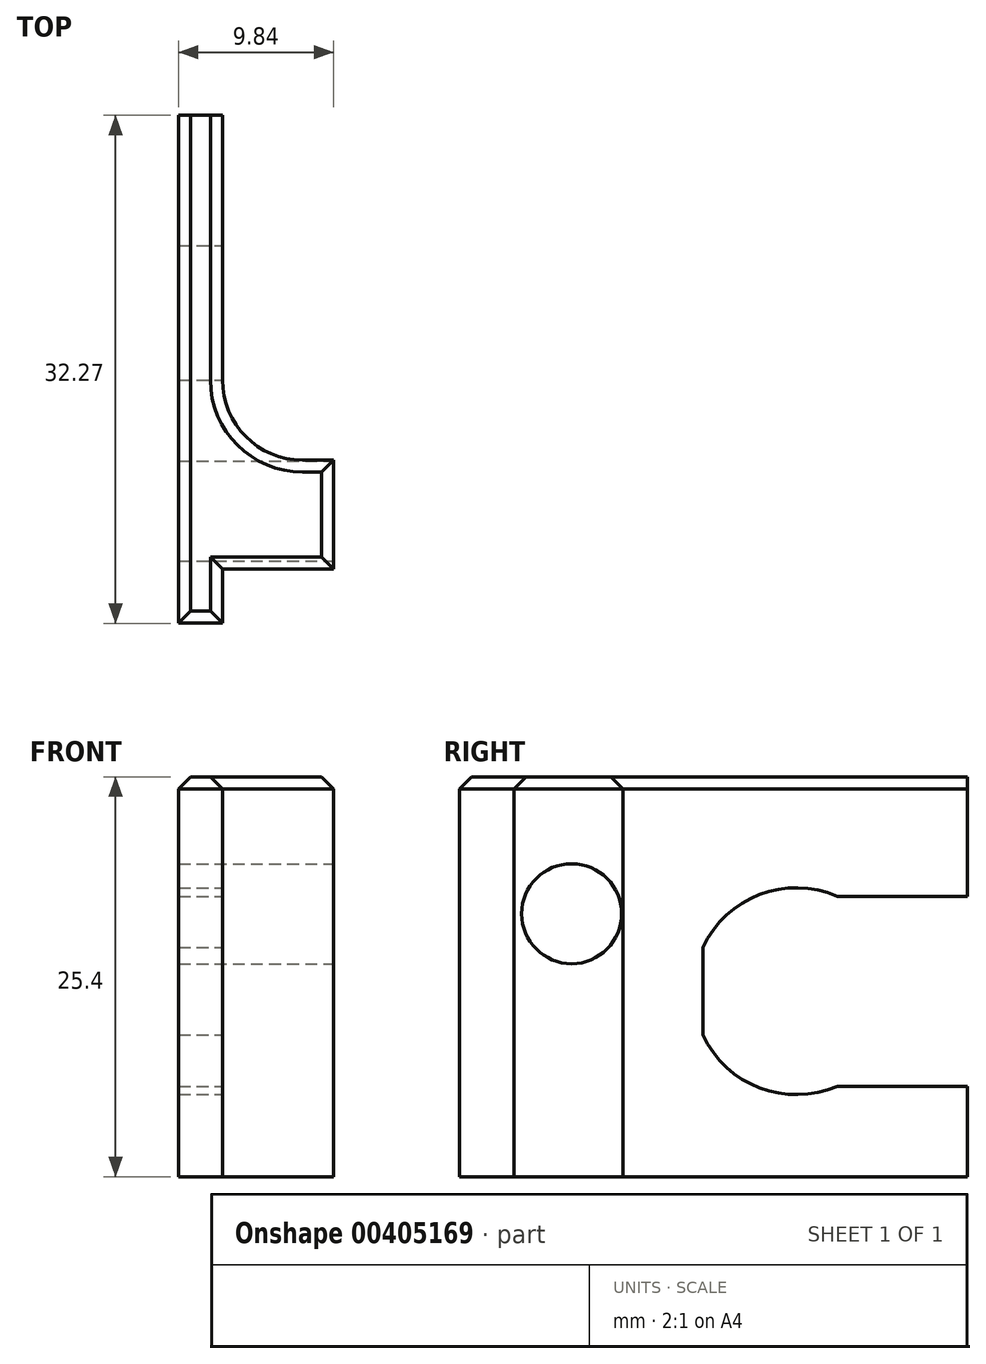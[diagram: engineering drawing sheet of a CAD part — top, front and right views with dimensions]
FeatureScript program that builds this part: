
annotation { "Feature Type Name" : "Feature", "Feature Type Description" : "" }
export const myFeature = defineFeature(function(context is Context, id is Id, definition is map)
    precondition{}
    {
        {
            var Q0;
            Q0=qCreatedBy(makeId("Top.planeOp"),FACE);
            var sketch = newSketch(context, id + "F0", { "sketchPlane" : qUnion([Q0])});
            skLineSegment(sketch, "E0.bottom", {"start": v(35.78, 48.25) * mm, "end": v(33, 48.25) * mm});
            skLineSegment(sketch, "E0.top", {"start": v(35.78, 15.98) * mm, "end": v(33, 15.98) * mm});
            skLineSegment(sketch, "E0.left", {"start": v(35.78, 48.25) * mm, "end": v(35.78, 26.35) * mm});
            skLineSegment(sketch, "E0.right", {"start": v(33, 48.25) * mm, "end": v(33, 15.98) * mm});
            skLineSegment(sketch, "E1.bottom", {"start": v(35.78, 26.35) * mm, "end": v(42.84, 26.35) * mm});
            skLineSegment(sketch, "E1.top", {"start": v(35.78, 19.43) * mm, "end": v(42.84, 19.43) * mm});
            skLineSegment(sketch, "E1.right", {"start": v(42.84, 26.35) * mm, "end": v(42.84, 19.43) * mm});
            skLineSegment(sketch, "E2.trimOffspring", {"start": v(35.78, 19.43) * mm, "end": v(35.78, 15.98) * mm});
            skSolve(sketch);
        }
        {
            var Q0;
            Q0 = qSketchRegion(id + "F0", true);
            extrude(context, id + "F1", {"entities" : qUnion([Q0]), "depth" : 25.4 * mm});
        }
        {
            var Q0;
            Q0=makeQuery(id+"F1.opExtrude","SWEPT_EDGE",EDGE,{"disambiguationData":[OSD([sQuery(id+"F0.wireOp",EDGE,"E0.left"),sQuery(id+"F0.wireOp",EDGE,"E1.bottom")])]});
            fillet(context, id + "F2", {"entities" : qUnion([Q0]), "radius" : 5.08 * mm, "tangentPropagation" : true, "allowEdgeOverflow" : false});
        }
        {
            var Q0;
            Q0=makeQuery(id+"F1.opExtrude","CAP_EDGE",EDGE,{"disambiguationData":[OSD([sQuery(id+"F0.wireOp",EDGE,"E0.left")])],"isStart":false});
            var Q1;
            Q1=makeQuery(id+"F1.opExtrude","CAP_EDGE",EDGE,{"disambiguationData":[OSD([sQuery(id+"F0.wireOp",EDGE,"E1.right")])],"isStart":false});
            var Q2;
            Q2=makeQuery(id+"F1.opExtrude","CAP_EDGE",EDGE,{"disambiguationData":[OSD([sQuery(id+"F0.wireOp",EDGE,"E1.top")])],"isStart":false});
            var Q3;
            Q3=makeQuery(id+"F1.opExtrude","CAP_EDGE",EDGE,{"disambiguationData":[OSD([sQuery(id+"F0.wireOp",EDGE,"E2.trimOffspring")])],"isStart":false});
            var Q4;
            Q4=makeQuery(id+"F1.opExtrude","CAP_EDGE",EDGE,{"disambiguationData":[OSD([sQuery(id+"F0.wireOp",EDGE,"E0.top")])],"isStart":false});
            var Q5;
            Q5=makeQuery(id+"F1.opExtrude","CAP_EDGE",EDGE,{"disambiguationData":[OSD([sQuery(id+"F0.wireOp",EDGE,"E0.right")])],"isStart":false});
            var Q6;
            {var subQ0=sQuery(id+"F0.wireOp",EDGE,"E1.bottom");var subQ1=sQuery(id+"F0.wireOp",EDGE,"E0.left");Q6=makeQuery(id+"F2.opFillet","BLEND_EDGE",EDGE,{"blendedFrom":[makeQuery(id+"F1.opExtrude","SWEPT_EDGE",EDGE,{"disambiguationData":[OSD([subQ1,subQ0])]}),makeQuery(id+"F1.opExtrude","CAP_FACE",FACE,{"disambiguationData":[OSD([sQuery(id+"F0.wireOp",EDGE,"E0.bottom"),sQuery(id+"F0.wireOp",EDGE,"E0.top"),subQ1,sQuery(id+"F0.wireOp",EDGE,"E0.right"),subQ0,sQuery(id+"F0.wireOp",EDGE,"E1.top"),sQuery(id+"F0.wireOp",EDGE,"E1.right"),sQuery(id+"F0.wireOp",EDGE,"E2.trimOffspring")])],"isStart":false})],"blendedInto":[makeQuery(id+"F1.opExtrude","CAP_FACE",FACE,{"disambiguationData":[OSD([sQuery(id+"F0.wireOp",EDGE,"E0.bottom"),sQuery(id+"F0.wireOp",EDGE,"E0.top"),subQ1,sQuery(id+"F0.wireOp",EDGE,"E0.right"),subQ0,sQuery(id+"F0.wireOp",EDGE,"E1.top"),sQuery(id+"F0.wireOp",EDGE,"E1.right"),sQuery(id+"F0.wireOp",EDGE,"E2.trimOffspring")])],"isStart":false})]});}
            var Q7;
            Q7=makeQuery(id+"F1.opExtrude","CAP_EDGE",EDGE,{"disambiguationData":[OSD([sQuery(id+"F0.wireOp",EDGE,"E1.bottom")])],"isStart":false});
            chamfer(context, id + "F3", {"entities" : qUnion([Q0, Q1, Q2, Q3, Q4, Q5, Q6, Q7]), "width" : 0.76 * mm, "tangentPropagation" : true});
        }
        {
            var Q0;
            Q0=makeQuery(id+"F1.opExtrude","SWEPT_FACE",FACE,{"disambiguationData":[OSD([sQuery(id+"F0.wireOp",EDGE,"E0.left")])]});
            var sketch = newSketch(context, id + "F4", { "sketchPlane" : qUnion([Q0])});
            skLineSegment(sketch, "E3.bottom", {"start": v(48.25, 17.81) * mm, "end": v(39.98, 17.81) * mm});
            skLineSegment(sketch, "E3.top", {"start": v(48.25, 5.75) * mm, "end": v(39.98, 5.75) * mm});
            skLineSegment(sketch, "E3.left", {"start": v(48.25, 17.81) * mm, "end": v(48.25, 5.75) * mm});
            skArc(sketch, "E4", {"start": v(39.98, 17.81) * mm, "mid": v(30.82, 11.78) * mm, "end": v(39.98, 5.75) * mm});
            skPoint(sketch, "E5.orphan", {"position": v(37.38, 5.75) * mm});
            skPoint(sketch, "E6.orphan", {"position": v(37.38, 17.81) * mm});
            skSolve(sketch);
        }
        {
            var Q0;
            {var subQ1=sQuery(id+"F4.wireOp",EDGE,"E3.bottom");Q0=makeQuery(id+"F4.imprint","IMPRINT",FACE,{"disambiguationData":[TD([[makeQuery(id+"F4.imprint","IMPRINT",EDGE,{"derivedFrom":subQ1}),1.0]])]});}
            extrude(context, id + "F5", {"entities" : qUnion([Q0]), "operationType" : NewBodyOperationType.REMOVE, "oppositeDirection" : true, "depth" : 25.4 * mm});
        }
        {
            var Q0;
            Q0=makeQuery(id+"F1.opExtrude","SWEPT_FACE",FACE,{"disambiguationData":[OSD([sQuery(id+"F0.wireOp",EDGE,"E1.right")])]});
            var sketch = newSketch(context, id + "F6", { "sketchPlane" : qUnion([Q0])});
            skCircle(sketch, "E7", {"center": v(23.1, 16.7) * mm, "radius": 1.64 * mm});
            skSolve(sketch);
        }
        {
            var Q0;
            Q0=sQuery(id+"F6.wireOp",VERTEX,"E7.center");
            var Q1;
            Q1=makeQuery(id+"F1.opExtrude","SWEPT_BODY",BODY,{"disambiguationData":[OSD([sQuery(id+"F0.wireOp",EDGE,"E0.bottom"),sQuery(id+"F0.wireOp",EDGE,"E0.top"),sQuery(id+"F0.wireOp",EDGE,"E0.left"),sQuery(id+"F0.wireOp",EDGE,"E0.right"),sQuery(id+"F0.wireOp",EDGE,"E1.bottom"),sQuery(id+"F0.wireOp",EDGE,"E1.top"),sQuery(id+"F0.wireOp",EDGE,"E1.right"),sQuery(id+"F0.wireOp",EDGE,"E2.trimOffspring")])]});
            hole(context, id + "F7", {"style" : HoleStyle.SIMPLE, "endStyle" : HoleEndStyle.THROUGH, "holeDiameter" : 6.35 * mm, "isTappedThrough" : true, "tappedDepth" : 12.7 * mm, "tapClearance" : 3, "locations" : qUnion([Q0]), "scope" : qUnion([Q1])});
        }
    });
